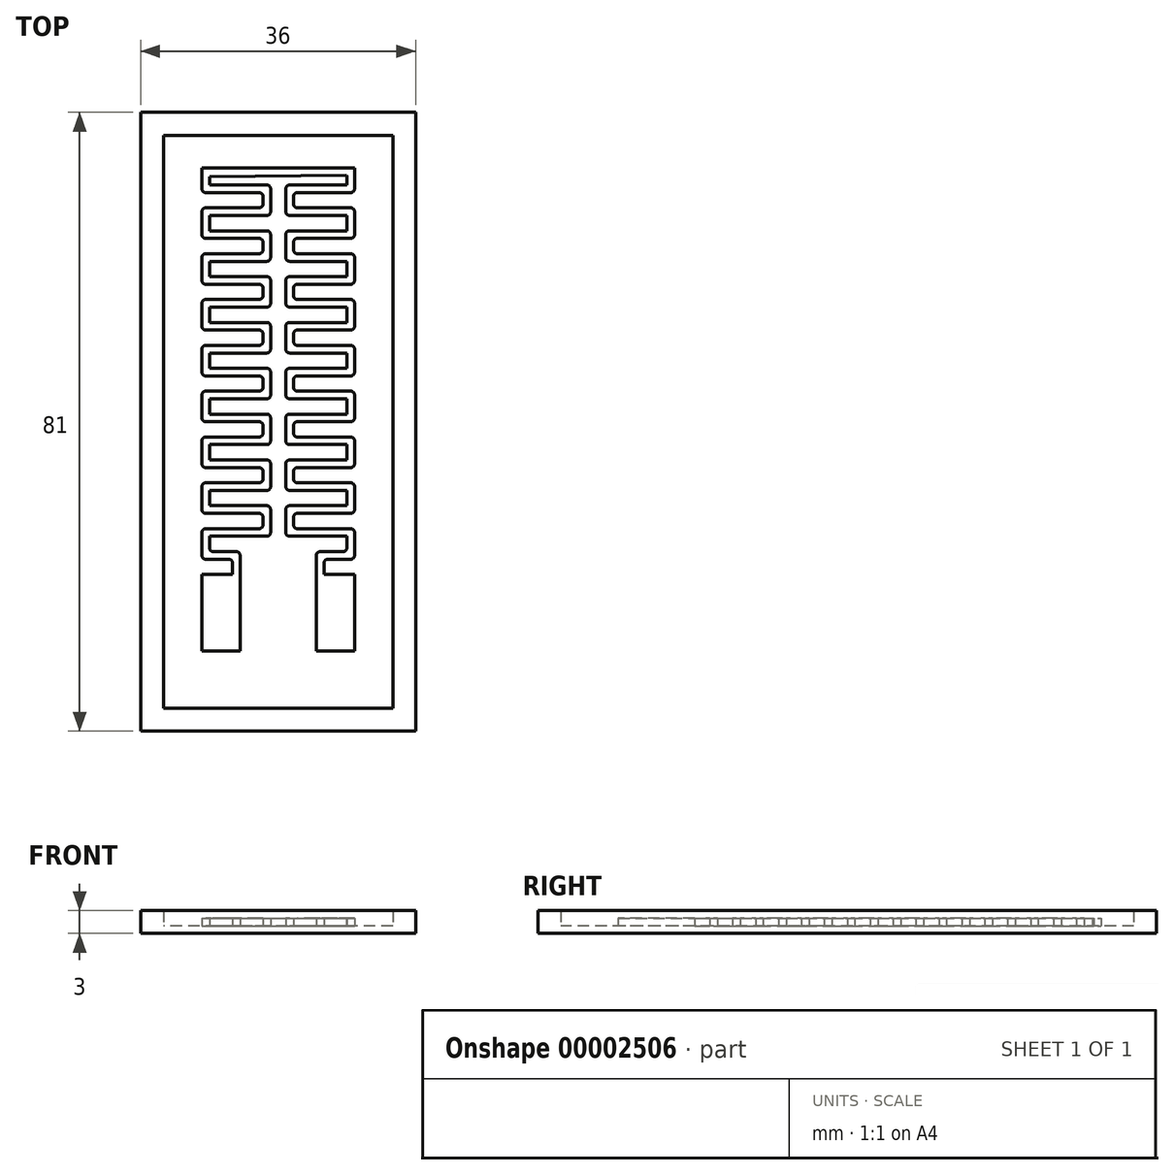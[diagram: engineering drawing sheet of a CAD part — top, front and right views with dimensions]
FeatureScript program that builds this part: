
annotation { "Feature Type Name" : "Feature", "Feature Type Description" : "" }
export const myFeature = defineFeature(function(context is Context, id is Id, definition is map)
    precondition{}
    {
        {
            var Q0;
            Q0=qCreatedBy(makeId("Top.planeOp"),FACE);
            var sketch = newSketch(context, id + "F0", { "sketchPlane" : qUnion([Q0])});
            skLineSegment(sketch, "E0.rect.bottom", {"start": v(15, 37.5) * mm, "end": v(-15, 37.5) * mm});
            skLineSegment(sketch, "E0.rect.top", {"start": v(15, -37.5) * mm, "end": v(-15, -37.5) * mm});
            skLineSegment(sketch, "E0.rect.left", {"start": v(15, 37.5) * mm, "end": v(15, -37.5) * mm});
            skLineSegment(sketch, "E0.rect.right", {"start": v(-15, 37.5) * mm, "end": v(-15, -37.5) * mm});
            skPoint(sketch, "E0.rect.middle", {"position": v(0, 0) * mm});
            skLineSegment(sketch, "E1", {"start": v(0, 0) * mm, "end": v(0, 17.9) * mm, "construction": true});
            skLineSegment(sketch, "E2.bottom", {"start": v(-10, -20) * mm, "end": v(-6, -20) * mm});
            skLineSegment(sketch, "E2.top", {"start": v(-10, -30) * mm, "end": v(-5, -30) * mm});
            skLineSegment(sketch, "E2.left", {"start": v(-10, -20) * mm, "end": v(-10, -30) * mm});
            skLineSegment(sketch, "E2.right", {"start": v(-5, -20) * mm, "end": v(-5, -30) * mm});
            skLineSegment(sketch, "E3", {"start": v(-5, -20) * mm, "end": v(-5, 28) * mm, "construction": true});
            skLineSegment(sketch, "E4", {"start": v(-4, 29) * mm, "end": v(0, 29) * mm, "construction": true});
            skLineSegment(sketch, "E5", {"start": v(-6, -20) * mm, "end": v(-6, 29) * mm, "construction": true});
            skLineSegment(sketch, "E6", {"start": v(-5, 30) * mm, "end": v(0, 30) * mm, "construction": true});
            skPoint(sketch, "E7.visualSharp", {"position": v(-6, 30) * mm});
            skArc(sketch, "E7.filletArc", {"start": v(-5, 30) * mm, "mid": v(-5.7, 29.7) * mm, "end": v(-6, 29) * mm, "construction": true});
            skArc(sketch, "E8.filletArc", {"start": v(-4, 29) * mm, "mid": v(-4.7, 28.7) * mm, "end": v(-5, 28) * mm, "construction": true});
            skLineSegment(sketch, "E9.0.MirrorCS", {"start": v(10, -30) * mm, "end": v(5, -30) * mm});
            skArc(sketch, "E9.1.MirrorCS", {"start": v(4, 29) * mm, "mid": v(4.7, 28.7) * mm, "end": v(5, 28) * mm, "construction": true});
            skArc(sketch, "E9.2.MirrorCS", {"start": v(5, 30) * mm, "mid": v(5.7, 29.7) * mm, "end": v(6, 29) * mm, "construction": true});
            skLineSegment(sketch, "E9.3.MirrorCS", {"start": v(10, -20) * mm, "end": v(6, -20) * mm});
            skLineSegment(sketch, "E9.4.MirrorCS", {"start": v(4, 29) * mm, "end": v(0, 29) * mm, "construction": true});
            skLineSegment(sketch, "E9.5.MirrorCS", {"start": v(5, 30) * mm, "end": v(0, 30) * mm, "construction": true});
            skPoint(sketch, "E9.6.MirrorP", {"position": v(6, 30) * mm});
            skLineSegment(sketch, "E9.8.MirrorCS", {"start": v(5, -20) * mm, "end": v(5, -30) * mm});
            skPoint(sketch, "E9.9.MirrorP", {"position": v(5, 29) * mm});
            skLineSegment(sketch, "E9.10.MirrorCS", {"start": v(6, -20) * mm, "end": v(6, 29) * mm, "construction": true});
            skLineSegment(sketch, "E9.11.MirrorCS", {"start": v(10, -20) * mm, "end": v(10, -30) * mm});
            skLineSegment(sketch, "E9.12.MirrorCS", {"start": v(5, -20) * mm, "end": v(5, 28) * mm, "construction": true});
            skLineSegment(sketch, "E10.0", {"start": v(18, 40.5) * mm, "end": v(-18, 40.5) * mm});
            skLineSegment(sketch, "E10.1", {"start": v(18, 40.5) * mm, "end": v(18, -40.5) * mm});
            skLineSegment(sketch, "E10.2", {"start": v(18, -40.5) * mm, "end": v(-18, -40.5) * mm});
            skLineSegment(sketch, "E10.3", {"start": v(-18, 40.5) * mm, "end": v(-18, -40.5) * mm});
            skLineSegment(sketch, "E11", {"start": v(-5, -20) * mm, "end": v(-5, -17.5) * mm});
            skLineSegment(sketch, "E12", {"start": v(-5.5, -17) * mm, "end": v(-8.5, -17) * mm});
            skLineSegment(sketch, "E13", {"start": v(-6, -20) * mm, "end": v(-6, -18.5) * mm});
            skLineSegment(sketch, "E14", {"start": v(-6.5, -18) * mm, "end": v(-9.5, -18) * mm});
            skLineSegment(sketch, "E15", {"start": v(-9, -16.5) * mm, "end": v(-9, -15) * mm});
            skLineSegment(sketch, "E16", {"start": v(-10, -17.5) * mm, "end": v(-10, -14.5) * mm});
            skLineSegment(sketch, "E17", {"start": v(0, 0) * mm, "end": v(0, -26.26) * mm, "construction": true});
            skLineSegment(sketch, "E18", {"start": v(-1, -22.87) * mm, "end": v(-1, 3.47) * mm, "construction": true});
            skLineSegment(sketch, "E19", {"start": v(-9, -15) * mm, "end": v(-1.5, -15) * mm});
            skLineSegment(sketch, "E20", {"start": v(-9.5, -14) * mm, "end": v(-2.5, -14) * mm});
            skLineSegment(sketch, "E21", {"start": v(-1, -14.5) * mm, "end": v(-1, -11.5) * mm});
            skLineSegment(sketch, "E22", {"start": v(-1.5, -11) * mm, "end": v(-9, -11) * mm});
            skLineSegment(sketch, "E23", {"start": v(-2, -13.5) * mm, "end": v(-2, -12.5) * mm});
            skLineSegment(sketch, "E24", {"start": v(-2.5, -12) * mm, "end": v(-9.5, -12) * mm});
            skLineSegment(sketch, "E25", {"start": v(-10, -11.5) * mm, "end": v(-10, -11) * mm});
            skPoint(sketch, "E26.visualSharp", {"position": v(-5, -17) * mm});
            skArc(sketch, "E26.filletArc", {"start": v(-5, -17.5) * mm, "mid": v(-5.15, -17.15) * mm, "end": v(-5.5, -17) * mm});
            skPoint(sketch, "E27.visualSharp", {"position": v(-6, -18) * mm});
            skArc(sketch, "E27.filletArc", {"start": v(-6, -18.5) * mm, "mid": v(-6.15, -18.15) * mm, "end": v(-6.5, -18) * mm});
            skPoint(sketch, "E28.visualSharp", {"position": v(-10, -18) * mm});
            skArc(sketch, "E28.filletArc", {"start": v(-10, -17.5) * mm, "mid": v(-9.85, -17.85) * mm, "end": v(-9.5, -18) * mm});
            skPoint(sketch, "E29.visualSharp", {"position": v(-10, -14) * mm});
            skArc(sketch, "E29.filletArc", {"start": v(-9.5, -14) * mm, "mid": v(-9.85, -14.15) * mm, "end": v(-10, -14.5) * mm});
            skPoint(sketch, "E30.visualSharp", {"position": v(-1, -15) * mm});
            skArc(sketch, "E30.filletArc", {"start": v(-1.5, -15) * mm, "mid": v(-1.15, -14.85) * mm, "end": v(-1, -14.5) * mm});
            skPoint(sketch, "E31.visualSharp", {"position": v(-2, -14) * mm});
            skArc(sketch, "E31.filletArc", {"start": v(-2.5, -14) * mm, "mid": v(-2.15, -13.85) * mm, "end": v(-2, -13.5) * mm});
            skPoint(sketch, "E32.visualSharp", {"position": v(-2, -12) * mm});
            skArc(sketch, "E32.filletArc", {"start": v(-2, -12.5) * mm, "mid": v(-2.15, -12.15) * mm, "end": v(-2.5, -12) * mm});
            skPoint(sketch, "E33.visualSharp", {"position": v(-1, -11) * mm});
            skArc(sketch, "E33.filletArc", {"start": v(-1, -11.5) * mm, "mid": v(-1.15, -11.15) * mm, "end": v(-1.5, -11) * mm});
            skPoint(sketch, "E34.visualSharp", {"position": v(-10, -12) * mm});
            skArc(sketch, "E34.filletArc", {"start": v(-10, -11.5) * mm, "mid": v(-9.85, -11.85) * mm, "end": v(-9.5, -12) * mm});
            skPoint(sketch, "E35.visualSharp", {"position": v(-9, -17) * mm});
            skArc(sketch, "E35.filletArc", {"start": v(-9, -16.5) * mm, "mid": v(-8.85, -16.85) * mm, "end": v(-8.5, -17) * mm});
            skLineSegment(sketch, "E36.0.1.0", {"start": v(-10, -11.5) * mm, "end": v(-10, -8.5) * mm});
            skPoint(sketch, "E36.0.1.1", {"position": v(-10, -8) * mm});
            skArc(sketch, "E36.0.1.2", {"start": v(-9.5, -8) * mm, "mid": v(-9.85, -8.15) * mm, "end": v(-10, -8.5) * mm});
            skLineSegment(sketch, "E36.0.1.3", {"start": v(-9, -9) * mm, "end": v(-1.5, -9) * mm});
            skLineSegment(sketch, "E36.0.1.4", {"start": v(-9.5, -8) * mm, "end": v(-2.5, -8) * mm});
            skArc(sketch, "E36.0.1.5", {"start": v(-1.5, -9) * mm, "mid": v(-1.15, -8.85) * mm, "end": v(-1, -8.5) * mm});
            skArc(sketch, "E36.0.1.6", {"start": v(-2.5, -8) * mm, "mid": v(-2.15, -7.85) * mm, "end": v(-2, -7.5) * mm});
            skLineSegment(sketch, "E36.0.1.7", {"start": v(-2, -7.5) * mm, "end": v(-2, -6.5) * mm});
            skLineSegment(sketch, "E36.0.1.8", {"start": v(-1, -8.5) * mm, "end": v(-1, -5.5) * mm});
            skArc(sketch, "E36.0.1.9", {"start": v(-1, -5.5) * mm, "mid": v(-1.15, -5.15) * mm, "end": v(-1.5, -5) * mm});
            skArc(sketch, "E36.0.1.10", {"start": v(-2, -6.5) * mm, "mid": v(-2.15, -6.15) * mm, "end": v(-2.5, -6) * mm});
            skLineSegment(sketch, "E36.0.1.11", {"start": v(-2.5, -6) * mm, "end": v(-9.5, -6) * mm});
            skLineSegment(sketch, "E36.0.1.12", {"start": v(-1.5, -5) * mm, "end": v(-9, -5) * mm});
            skArc(sketch, "E36.0.1.13", {"start": v(-10, -5.5) * mm, "mid": v(-9.85, -5.85) * mm, "end": v(-9.5, -6) * mm});
            skLineSegment(sketch, "E36.0.1.14", {"start": v(-10, -5.5) * mm, "end": v(-10, -5) * mm});
            skLineSegment(sketch, "E36.0.2.0", {"start": v(-10, -5.5) * mm, "end": v(-10, -2.5) * mm});
            skPoint(sketch, "E36.0.2.1", {"position": v(-10, -2) * mm});
            skArc(sketch, "E36.0.2.2", {"start": v(-9.5, -2) * mm, "mid": v(-9.85, -2.15) * mm, "end": v(-10, -2.5) * mm});
            skLineSegment(sketch, "E36.0.2.3", {"start": v(-9, -3) * mm, "end": v(-1.5, -3) * mm});
            skLineSegment(sketch, "E36.0.2.4", {"start": v(-9.5, -2) * mm, "end": v(-2.5, -2) * mm});
            skArc(sketch, "E36.0.2.5", {"start": v(-1.5, -3) * mm, "mid": v(-1.15, -2.85) * mm, "end": v(-1, -2.5) * mm});
            skArc(sketch, "E36.0.2.6", {"start": v(-2.5, -2) * mm, "mid": v(-2.15, -1.85) * mm, "end": v(-2, -1.5) * mm});
            skLineSegment(sketch, "E36.0.2.7", {"start": v(-2, -1.5) * mm, "end": v(-2, -0.5) * mm});
            skLineSegment(sketch, "E36.0.2.8", {"start": v(-1, -2.5) * mm, "end": v(-1, 0.5) * mm});
            skArc(sketch, "E36.0.2.9", {"start": v(-1, 0.5) * mm, "mid": v(-1.15, 0.85) * mm, "end": v(-1.5, 1) * mm});
            skArc(sketch, "E36.0.2.10", {"start": v(-2, -0.5) * mm, "mid": v(-2.15, -0.15) * mm, "end": v(-2.5, 0) * mm});
            skLineSegment(sketch, "E36.0.2.11", {"start": v(-2.5, 0) * mm, "end": v(-9.5, 0) * mm});
            skLineSegment(sketch, "E36.0.2.12", {"start": v(-1.5, 1) * mm, "end": v(-9, 1) * mm});
            skArc(sketch, "E36.0.2.13", {"start": v(-10, 0.5) * mm, "mid": v(-9.85, 0.15) * mm, "end": v(-9.5, 0) * mm});
            skLineSegment(sketch, "E36.0.2.14", {"start": v(-10, 0.5) * mm, "end": v(-10, 1) * mm});
            skLineSegment(sketch, "E36.0.3.0", {"start": v(-10, 0.5) * mm, "end": v(-10, 3.5) * mm});
            skPoint(sketch, "E36.0.3.1", {"position": v(-10, 4) * mm});
            skArc(sketch, "E36.0.3.2", {"start": v(-9.5, 4) * mm, "mid": v(-9.85, 3.85) * mm, "end": v(-10, 3.5) * mm});
            skLineSegment(sketch, "E36.0.3.3", {"start": v(-9, 3) * mm, "end": v(-1.5, 3) * mm});
            skLineSegment(sketch, "E36.0.3.4", {"start": v(-9.5, 4) * mm, "end": v(-2.5, 4) * mm});
            skArc(sketch, "E36.0.3.5", {"start": v(-1.5, 3) * mm, "mid": v(-1.15, 3.15) * mm, "end": v(-1, 3.5) * mm});
            skArc(sketch, "E36.0.3.6", {"start": v(-2.5, 4) * mm, "mid": v(-2.15, 4.15) * mm, "end": v(-2, 4.5) * mm});
            skLineSegment(sketch, "E36.0.3.7", {"start": v(-2, 4.5) * mm, "end": v(-2, 5.5) * mm});
            skLineSegment(sketch, "E36.0.3.8", {"start": v(-1, 3.5) * mm, "end": v(-1, 6.5) * mm});
            skArc(sketch, "E36.0.3.9", {"start": v(-1, 6.5) * mm, "mid": v(-1.15, 6.85) * mm, "end": v(-1.5, 7) * mm});
            skArc(sketch, "E36.0.3.10", {"start": v(-2, 5.5) * mm, "mid": v(-2.15, 5.85) * mm, "end": v(-2.5, 6) * mm});
            skLineSegment(sketch, "E36.0.3.11", {"start": v(-2.5, 6) * mm, "end": v(-9.5, 6) * mm});
            skLineSegment(sketch, "E36.0.3.12", {"start": v(-1.5, 7) * mm, "end": v(-9, 7) * mm});
            skArc(sketch, "E36.0.3.13", {"start": v(-10, 6.5) * mm, "mid": v(-9.85, 6.15) * mm, "end": v(-9.5, 6) * mm});
            skLineSegment(sketch, "E36.0.3.14", {"start": v(-10, 6.5) * mm, "end": v(-10, 7) * mm});
            skLineSegment(sketch, "E36.0.4.0", {"start": v(-10, 6.5) * mm, "end": v(-10, 9.5) * mm});
            skPoint(sketch, "E36.0.4.1", {"position": v(-10, 10) * mm});
            skArc(sketch, "E36.0.4.2", {"start": v(-9.5, 10) * mm, "mid": v(-9.85, 9.85) * mm, "end": v(-10, 9.5) * mm});
            skLineSegment(sketch, "E36.0.4.3", {"start": v(-9, 9) * mm, "end": v(-1.5, 9) * mm});
            skLineSegment(sketch, "E36.0.4.4", {"start": v(-9.5, 10) * mm, "end": v(-2.5, 10) * mm});
            skArc(sketch, "E36.0.4.5", {"start": v(-1.5, 9) * mm, "mid": v(-1.15, 9.15) * mm, "end": v(-1, 9.5) * mm});
            skArc(sketch, "E36.0.4.6", {"start": v(-2.5, 10) * mm, "mid": v(-2.15, 10.15) * mm, "end": v(-2, 10.5) * mm});
            skLineSegment(sketch, "E36.0.4.7", {"start": v(-2, 10.5) * mm, "end": v(-2, 11.5) * mm});
            skLineSegment(sketch, "E36.0.4.8", {"start": v(-1, 9.5) * mm, "end": v(-1, 12.5) * mm});
            skArc(sketch, "E36.0.4.9", {"start": v(-1, 12.5) * mm, "mid": v(-1.15, 12.85) * mm, "end": v(-1.5, 13) * mm});
            skArc(sketch, "E36.0.4.10", {"start": v(-2, 11.5) * mm, "mid": v(-2.15, 11.85) * mm, "end": v(-2.5, 12) * mm});
            skLineSegment(sketch, "E36.0.4.11", {"start": v(-2.5, 12) * mm, "end": v(-9.5, 12) * mm});
            skLineSegment(sketch, "E36.0.4.12", {"start": v(-1.5, 13) * mm, "end": v(-9, 13) * mm});
            skArc(sketch, "E36.0.4.13", {"start": v(-10, 12.5) * mm, "mid": v(-9.85, 12.15) * mm, "end": v(-9.5, 12) * mm});
            skLineSegment(sketch, "E36.0.4.14", {"start": v(-10, 12.5) * mm, "end": v(-10, 13) * mm});
            skLineSegment(sketch, "E36.direction1", {"start": v(-10, -17.5) * mm, "end": v(15, -17.5) * mm, "construction": true});
            skLineSegment(sketch, "E36.direction2", {"start": v(-10, -17.5) * mm, "end": v(-10, -11.5) * mm, "construction": true});
            skArc(sketch, "E37.0.MirrorCS", {"start": v(10, -11.5) * mm, "mid": v(9.85, -11.85) * mm, "end": v(9.5, -12) * mm});
            skLineSegment(sketch, "E37.1.MirrorCS", {"start": v(10, -11.5) * mm, "end": v(10, -11) * mm});
            skArc(sketch, "E37.2.MirrorCS", {"start": v(10, -17.5) * mm, "mid": v(9.85, -17.85) * mm, "end": v(9.5, -18) * mm});
            skArc(sketch, "E37.3.MirrorCS", {"start": v(9, -16.5) * mm, "mid": v(8.85, -16.85) * mm, "end": v(8.5, -17) * mm});
            skArc(sketch, "E37.4.MirrorCS", {"start": v(1.5, 3) * mm, "mid": v(1.15, 3.15) * mm, "end": v(1, 3.5) * mm});
            skArc(sketch, "E37.5.MirrorCS", {"start": v(2.5, 16) * mm, "mid": v(2.15, 16.15) * mm, "end": v(2, 16.5) * mm});
            skLineSegment(sketch, "E37.6.MirrorCS", {"start": v(10, -5.5) * mm, "end": v(10, -5) * mm});
            skLineSegment(sketch, "E37.7.MirrorCS", {"start": v(2, 16.5) * mm, "end": v(2, 17.5) * mm});
            skLineSegment(sketch, "E37.8.MirrorCS", {"start": v(2, 4.5) * mm, "end": v(2, 5.5) * mm});
            skArc(sketch, "E37.9.MirrorCS", {"start": v(10, 24.5) * mm, "mid": v(9.85, 24.15) * mm, "end": v(9.5, 24) * mm});
            skLineSegment(sketch, "E37.10.MirrorCS", {"start": v(10, 24.5) * mm, "end": v(10, 25) * mm});
            skArc(sketch, "E37.11.MirrorCS", {"start": v(2.5, -14) * mm, "mid": v(2.15, -13.85) * mm, "end": v(2, -13.5) * mm});
            skArc(sketch, "E37.12.MirrorCS", {"start": v(1.5, -15) * mm, "mid": v(1.15, -14.85) * mm, "end": v(1, -14.5) * mm});
            skArc(sketch, "E37.13.MirrorCS", {"start": v(10, 0.5) * mm, "mid": v(9.85, 0.15) * mm, "end": v(9.5, 0) * mm});
            skLineSegment(sketch, "E37.14.MirrorCS", {"start": v(10, 0.5) * mm, "end": v(10, 1) * mm});
            skArc(sketch, "E37.15.MirrorCS", {"start": v(10, -5.5) * mm, "mid": v(9.85, -5.85) * mm, "end": v(9.5, -6) * mm});
            skArc(sketch, "E37.16.MirrorCS", {"start": v(10, 18.5) * mm, "mid": v(9.85, 18.15) * mm, "end": v(9.5, 18) * mm});
            skLineSegment(sketch, "E37.17.MirrorCS", {"start": v(10, 18.5) * mm, "end": v(10, 19) * mm});
            skArc(sketch, "E37.18.MirrorCS", {"start": v(2, 5.5) * mm, "mid": v(2.15, 5.85) * mm, "end": v(2.5, 6) * mm});
            skLineSegment(sketch, "E37.19.MirrorCS", {"start": v(10, 12.5) * mm, "end": v(10, 13) * mm});
            skArc(sketch, "E37.20.MirrorCS", {"start": v(1, -5.5) * mm, "mid": v(1.15, -5.15) * mm, "end": v(1.5, -5) * mm});
            skArc(sketch, "E37.21.MirrorCS", {"start": v(10, 6.5) * mm, "mid": v(9.85, 6.15) * mm, "end": v(9.5, 6) * mm});
            skArc(sketch, "E37.22.MirrorCS", {"start": v(2.5, 4) * mm, "mid": v(2.15, 4.15) * mm, "end": v(2, 4.5) * mm});
            skArc(sketch, "E37.23.MirrorCS", {"start": v(10, 12.5) * mm, "mid": v(9.85, 12.15) * mm, "end": v(9.5, 12) * mm});
            skLineSegment(sketch, "E37.24.MirrorCS", {"start": v(10, 6.5) * mm, "end": v(10, 7) * mm});
            skArc(sketch, "E37.25.MirrorCS", {"start": v(2, -6.5) * mm, "mid": v(2.15, -6.15) * mm, "end": v(2.5, -6) * mm});
            skArc(sketch, "E37.26.MirrorCS", {"start": v(2, 23.5) * mm, "mid": v(2.15, 23.85) * mm, "end": v(2.5, 24) * mm});
            skArc(sketch, "E37.27.MirrorCS", {"start": v(2.5, 10) * mm, "mid": v(2.15, 10.15) * mm, "end": v(2, 10.5) * mm});
            skArc(sketch, "E37.28.MirrorCS", {"start": v(9.5, -2) * mm, "mid": v(9.85, -2.15) * mm, "end": v(10, -2.5) * mm});
            skArc(sketch, "E37.29.MirrorCS", {"start": v(10, 30.5) * mm, "mid": v(9.85, 30.15) * mm, "end": v(9.5, 30) * mm});
            skArc(sketch, "E37.30.MirrorCS", {"start": v(1, 18.5) * mm, "mid": v(1.15, 18.85) * mm, "end": v(1.5, 19) * mm});
            skLineSegment(sketch, "E37.31.MirrorCS", {"start": v(2, 10.5) * mm, "end": v(2, 11.5) * mm});
            skArc(sketch, "E37.32.MirrorCS", {"start": v(2, 29.5) * mm, "mid": v(2.15, 29.85) * mm, "end": v(2.5, 30) * mm});
            skArc(sketch, "E37.33.MirrorCS", {"start": v(1, -11.5) * mm, "mid": v(1.15, -11.15) * mm, "end": v(1.5, -11) * mm});
            skArc(sketch, "E37.34.MirrorCS", {"start": v(9.5, 4) * mm, "mid": v(9.85, 3.85) * mm, "end": v(10, 3.5) * mm});
            skArc(sketch, "E37.35.MirrorCS", {"start": v(1.5, 9) * mm, "mid": v(1.15, 9.15) * mm, "end": v(1, 9.5) * mm});
            skArc(sketch, "E37.36.MirrorCS", {"start": v(1, 24.5) * mm, "mid": v(1.15, 24.85) * mm, "end": v(1.5, 25) * mm});
            skLineSegment(sketch, "E37.37.MirrorCS", {"start": v(10, 30.5) * mm, "end": v(10, 31) * mm});
            skArc(sketch, "E37.40.MirrorCS", {"start": v(1.5, -3) * mm, "mid": v(1.15, -2.85) * mm, "end": v(1, -2.5) * mm});
            skArc(sketch, "E37.41.MirrorCS", {"start": v(1, 12.5) * mm, "mid": v(1.15, 12.85) * mm, "end": v(1.5, 13) * mm});
            skLineSegment(sketch, "E37.42.MirrorCS", {"start": v(2, -13.5) * mm, "end": v(2, -12.5) * mm});
            skArc(sketch, "E37.43.MirrorCS", {"start": v(2.5, -2) * mm, "mid": v(2.15, -1.85) * mm, "end": v(2, -1.5) * mm});
            skArc(sketch, "E37.44.MirrorCS", {"start": v(2, 11.5) * mm, "mid": v(2.15, 11.85) * mm, "end": v(2.5, 12) * mm});
            skLineSegment(sketch, "E37.45.MirrorCS", {"start": v(9, -16.5) * mm, "end": v(9, -15) * mm});
            skArc(sketch, "E37.46.MirrorCS", {"start": v(9.5, 22) * mm, "mid": v(9.85, 21.85) * mm, "end": v(10, 21.5) * mm});
            skArc(sketch, "E37.47.MirrorCS", {"start": v(9.5, 28) * mm, "mid": v(9.85, 27.85) * mm, "end": v(10, 27.5) * mm});
            skArc(sketch, "E37.48.MirrorCS", {"start": v(1, 6.5) * mm, "mid": v(1.15, 6.85) * mm, "end": v(1.5, 7) * mm});
            skArc(sketch, "E37.49.MirrorCS", {"start": v(6, -18.5) * mm, "mid": v(6.15, -18.15) * mm, "end": v(6.5, -18) * mm});
            skArc(sketch, "E37.50.MirrorCS", {"start": v(9.5, 10) * mm, "mid": v(9.85, 9.85) * mm, "end": v(10, 9.5) * mm});
            skArc(sketch, "E37.51.MirrorCS", {"start": v(2.5, 22) * mm, "mid": v(2.15, 22.15) * mm, "end": v(2, 22.5) * mm});
            skLineSegment(sketch, "E37.52.MirrorCS", {"start": v(2, -1.5) * mm, "end": v(2, -0.5) * mm});
            skArc(sketch, "E37.53.MirrorCS", {"start": v(2, -0.5) * mm, "mid": v(2.15, -0.15) * mm, "end": v(2.5, 0) * mm});
            skArc(sketch, "E37.54.MirrorCS", {"start": v(2, -12.5) * mm, "mid": v(2.15, -12.15) * mm, "end": v(2.5, -12) * mm});
            skArc(sketch, "E37.55.MirrorCS", {"start": v(2.5, -8) * mm, "mid": v(2.15, -7.85) * mm, "end": v(2, -7.5) * mm});
            skArc(sketch, "E37.56.MirrorCS", {"start": v(1.5, -9) * mm, "mid": v(1.15, -8.85) * mm, "end": v(1, -8.5) * mm});
            skArc(sketch, "E37.57.MirrorCS", {"start": v(5, -17.5) * mm, "mid": v(5.15, -17.15) * mm, "end": v(5.5, -17) * mm});
            skLineSegment(sketch, "E37.58.MirrorCS", {"start": v(2, 22.5) * mm, "end": v(2, 23.5) * mm});
            skArc(sketch, "E37.59.MirrorCS", {"start": v(1.5, 27) * mm, "mid": v(1.15, 27.15) * mm, "end": v(1, 27.5) * mm});
            skArc(sketch, "E37.60.MirrorCS", {"start": v(9.5, -8) * mm, "mid": v(9.85, -8.15) * mm, "end": v(10, -8.5) * mm});
            skArc(sketch, "E37.61.MirrorCS", {"start": v(2, 17.5) * mm, "mid": v(2.15, 17.85) * mm, "end": v(2.5, 18) * mm});
            skLineSegment(sketch, "E37.62.MirrorCS", {"start": v(2, -7.5) * mm, "end": v(2, -6.5) * mm});
            skArc(sketch, "E37.63.MirrorCS", {"start": v(1, 0.5) * mm, "mid": v(1.15, 0.85) * mm, "end": v(1.5, 1) * mm});
            skArc(sketch, "E37.64.MirrorCS", {"start": v(2.5, 28) * mm, "mid": v(2.15, 28.15) * mm, "end": v(2, 28.5) * mm});
            skArc(sketch, "E37.65.MirrorCS", {"start": v(9.5, 16) * mm, "mid": v(9.85, 15.85) * mm, "end": v(10, 15.5) * mm});
            skArc(sketch, "E37.66.MirrorCS", {"start": v(9.5, -14) * mm, "mid": v(9.85, -14.15) * mm, "end": v(10, -14.5) * mm});
            skLineSegment(sketch, "E37.67.MirrorCS", {"start": v(2, 28.5) * mm, "end": v(2, 29.5) * mm});
            skArc(sketch, "E37.68.MirrorCS", {"start": v(1.5, 21) * mm, "mid": v(1.15, 21.15) * mm, "end": v(1, 21.5) * mm});
            skArc(sketch, "E37.69.MirrorCS", {"start": v(1, 30.5) * mm, "mid": v(1.15, 30.85) * mm, "end": v(1.5, 31) * mm});
            skArc(sketch, "E37.70.MirrorCS", {"start": v(1.5, 15) * mm, "mid": v(1.15, 15.15) * mm, "end": v(1, 15.5) * mm});
            skLineSegment(sketch, "E37.74.MirrorCS", {"start": v(10, -17.5) * mm, "end": v(10, -11.5) * mm, "construction": true});
            skLineSegment(sketch, "E37.75.MirrorCS", {"start": v(1, -14.5) * mm, "end": v(1, -11.5) * mm});
            skPoint(sketch, "E37.77.MirrorP", {"position": v(10, 22) * mm});
            skLineSegment(sketch, "E37.78.MirrorCS", {"start": v(1.5, 31) * mm, "end": v(9, 31) * mm});
            skLineSegment(sketch, "E37.79.MirrorCS", {"start": v(1, 15.5) * mm, "end": v(1, 18.5) * mm});
            skLineSegment(sketch, "E37.80.MirrorCS", {"start": v(9.5, 4) * mm, "end": v(2.5, 4) * mm});
            skLineSegment(sketch, "E37.81.MirrorCS", {"start": v(9, -15) * mm, "end": v(1.5, -15) * mm});
            skPoint(sketch, "E37.82.MirrorP", {"position": v(1, -15) * mm});
            skLineSegment(sketch, "E37.83.MirrorCS", {"start": v(9, -3) * mm, "end": v(1.5, -3) * mm});
            skLineSegment(sketch, "E37.84.MirrorCS", {"start": v(10, -11.5) * mm, "end": v(10, -8.5) * mm});
            skLineSegment(sketch, "E37.85.MirrorCS", {"start": v(9.5, -14) * mm, "end": v(2.5, -14) * mm});
            skLineSegment(sketch, "E37.86.MirrorCS", {"start": v(2.5, 24) * mm, "end": v(9.5, 24) * mm});
            skLineSegment(sketch, "E37.87.MirrorCS", {"start": v(9.5, 10) * mm, "end": v(2.5, 10) * mm});
            skLineSegment(sketch, "E37.88.MirrorCS", {"start": v(1, 21.5) * mm, "end": v(1, 24.5) * mm});
            skPoint(sketch, "E37.90.MirrorP", {"position": v(10, -14) * mm});
            skLineSegment(sketch, "E37.91.MirrorCS", {"start": v(2.5, 30) * mm, "end": v(9.5, 30) * mm});
            skLineSegment(sketch, "E37.92.MirrorCS", {"start": v(9, 3) * mm, "end": v(1.5, 3) * mm});
            skLineSegment(sketch, "E37.93.MirrorCS", {"start": v(10, -5.5) * mm, "end": v(10, -2.5) * mm});
            skLineSegment(sketch, "E37.94.MirrorCS", {"start": v(1.5, 25) * mm, "end": v(9, 25) * mm});
            skPoint(sketch, "E37.95.MirrorP", {"position": v(2, -14) * mm});
            skLineSegment(sketch, "E37.96.MirrorCS", {"start": v(2.5, 18) * mm, "end": v(9.5, 18) * mm});
            skLineSegment(sketch, "E37.97.MirrorCS", {"start": v(9, -9) * mm, "end": v(1.5, -9) * mm});
            skLineSegment(sketch, "E37.98.MirrorCS", {"start": v(1.5, -11) * mm, "end": v(9, -11) * mm});
            skPoint(sketch, "E37.99.MirrorP", {"position": v(10, -2) * mm});
            skLineSegment(sketch, "E37.100.MirrorCS", {"start": v(9.5, -8) * mm, "end": v(2.5, -8) * mm});
            skLineSegment(sketch, "E37.101.MirrorCS", {"start": v(1, 3.5) * mm, "end": v(1, 6.5) * mm});
            skLineSegment(sketch, "E37.102.MirrorCS", {"start": v(1.5, 19) * mm, "end": v(9, 19) * mm});
            skLineSegment(sketch, "E37.103.MirrorCS", {"start": v(1.5, -5) * mm, "end": v(9, -5) * mm});
            skLineSegment(sketch, "E37.104.MirrorCS", {"start": v(2.5, 12) * mm, "end": v(9.5, 12) * mm});
            skLineSegment(sketch, "E37.105.MirrorCS", {"start": v(1.5, 13) * mm, "end": v(9, 13) * mm});
            skLineSegment(sketch, "E37.106.MirrorCS", {"start": v(10, 0.5) * mm, "end": v(10, 3.5) * mm});
            skLineSegment(sketch, "E37.107.MirrorCS", {"start": v(10, -17.5) * mm, "end": v(10, -14.5) * mm});
            skLineSegment(sketch, "E37.108.MirrorCS", {"start": v(10, 24.5) * mm, "end": v(10, 27.5) * mm});
            skPoint(sketch, "E37.109.MirrorP", {"position": v(2, -12) * mm});
            skLineSegment(sketch, "E37.110.MirrorCS", {"start": v(9.5, 28) * mm, "end": v(2.5, 28) * mm});
            skLineSegment(sketch, "E37.111.MirrorCS", {"start": v(1, -8.5) * mm, "end": v(1, -5.5) * mm});
            skLineSegment(sketch, "E37.112.MirrorCS", {"start": v(6.5, -18) * mm, "end": v(9.5, -18) * mm});
            skLineSegment(sketch, "E37.113.MirrorCS", {"start": v(2.5, -6) * mm, "end": v(9.5, -6) * mm});
            skPoint(sketch, "E37.114.MirrorP", {"position": v(9, -17) * mm});
            skLineSegment(sketch, "E37.115.MirrorCS", {"start": v(1, 27.5) * mm, "end": v(1, 30.5) * mm});
            skPoint(sketch, "E37.116.MirrorP", {"position": v(6, -18) * mm});
            skLineSegment(sketch, "E37.117.MirrorCS", {"start": v(9.5, 16) * mm, "end": v(2.5, 16) * mm});
            skPoint(sketch, "E37.118.MirrorP", {"position": v(10, 4) * mm});
            skLineSegment(sketch, "E37.119.MirrorCS", {"start": v(1, -2.5) * mm, "end": v(1, 0.5) * mm});
            skLineSegment(sketch, "E37.120.MirrorCS", {"start": v(1.5, 7) * mm, "end": v(9, 7) * mm});
            skPoint(sketch, "E37.121.MirrorP", {"position": v(10, -8) * mm});
            skPoint(sketch, "E37.122.MirrorP", {"position": v(10, -18) * mm});
            skLineSegment(sketch, "E37.123.MirrorCS", {"start": v(2.5, -12) * mm, "end": v(9.5, -12) * mm});
            skLineSegment(sketch, "E37.124.MirrorCS", {"start": v(10, 6.5) * mm, "end": v(10, 9.5) * mm});
            skLineSegment(sketch, "E37.125.MirrorCS", {"start": v(10, 18.5) * mm, "end": v(10, 21.5) * mm});
            skPoint(sketch, "E37.126.MirrorP", {"position": v(10, 16) * mm});
            skPoint(sketch, "E37.127.MirrorP", {"position": v(10, -12) * mm});
            skLineSegment(sketch, "E37.128.MirrorCS", {"start": v(9, 9) * mm, "end": v(1.5, 9) * mm});
            skPoint(sketch, "E37.129.MirrorP", {"position": v(5, -17) * mm});
            skLineSegment(sketch, "E37.130.MirrorCS", {"start": v(5.5, -17) * mm, "end": v(8.5, -17) * mm});
            skLineSegment(sketch, "E37.131.MirrorCS", {"start": v(2.5, 0) * mm, "end": v(9.5, 0) * mm});
            skLineSegment(sketch, "E37.132.MirrorCS", {"start": v(10, 12.5) * mm, "end": v(10, 15.5) * mm});
            skLineSegment(sketch, "E37.133.MirrorCS", {"start": v(9, 21) * mm, "end": v(1.5, 21) * mm});
            skLineSegment(sketch, "E37.134.MirrorCS", {"start": v(1, 9.5) * mm, "end": v(1, 12.5) * mm});
            skLineSegment(sketch, "E37.135.MirrorCS", {"start": v(9.5, -2) * mm, "end": v(2.5, -2) * mm});
            skPoint(sketch, "E37.136.MirrorP", {"position": v(10, 10) * mm});
            skLineSegment(sketch, "E37.138.MirrorCS", {"start": v(9, 27) * mm, "end": v(1.5, 27) * mm});
            skLineSegment(sketch, "E37.139.MirrorCS", {"start": v(2.5, 6) * mm, "end": v(9.5, 6) * mm});
            skLineSegment(sketch, "E37.140.MirrorCS", {"start": v(9.5, 22) * mm, "end": v(2.5, 22) * mm});
            skLineSegment(sketch, "E37.141.MirrorCS", {"start": v(9, 15) * mm, "end": v(1.5, 15) * mm});
            skLineSegment(sketch, "E37.142.MirrorCS", {"start": v(1.5, 1) * mm, "end": v(9, 1) * mm});
            skPoint(sketch, "E37.143.MirrorP", {"position": v(10, 28) * mm});
            skPoint(sketch, "E37.144.MirrorP", {"position": v(1, -11) * mm});
            skLineSegment(sketch, "E38", {"start": v(-10, 31) * mm, "end": v(-10, 33.22) * mm});
            skLineSegment(sketch, "E39", {"start": v(-10, 33.22) * mm, "end": v(7.5, 33.22) * mm});
            skLineSegment(sketch, "E40", {"start": v(-9, 31) * mm, "end": v(-9, 32.11) * mm});
            skLineSegment(sketch, "E41", {"start": v(-9, 32.11) * mm, "end": v(9.03, 32.26) * mm});
            skLineSegment(sketch, "E42", {"start": v(10, 31) * mm, "end": v(10, 33.22) * mm});
            skLineSegment(sketch, "E43", {"start": v(9, 31) * mm, "end": v(9.03, 32.26) * mm});
            skLineSegment(sketch, "E44", {"start": v(10, 33.22) * mm, "end": v(7.5, 33.22) * mm});
            skLineSegment(sketch, "E45", {"start": v(9, 27) * mm, "end": v(9, 25) * mm});
            skLineSegment(sketch, "E46", {"start": v(-9, 27) * mm, "end": v(-9, 25) * mm});
            skLineSegment(sketch, "E47", {"start": v(9, 21) * mm, "end": v(9, 19) * mm});
            skLineSegment(sketch, "E48", {"start": v(-9, 21) * mm, "end": v(-9, 19) * mm});
            skLineSegment(sketch, "E49", {"start": v(-9, 15) * mm, "end": v(-9, 13) * mm});
            skLineSegment(sketch, "E50", {"start": v(9, 15) * mm, "end": v(9, 13) * mm});
            skLineSegment(sketch, "E51", {"start": v(9, 9) * mm, "end": v(9, 7) * mm});
            skLineSegment(sketch, "E52", {"start": v(-9, 9) * mm, "end": v(-9, 7) * mm});
            skLineSegment(sketch, "E53", {"start": v(-9, 3) * mm, "end": v(-9, 1) * mm});
            skLineSegment(sketch, "E54", {"start": v(9, 3) * mm, "end": v(9, 1) * mm});
            skLineSegment(sketch, "E55", {"start": v(9, -3) * mm, "end": v(9, -5) * mm});
            skLineSegment(sketch, "E56", {"start": v(-9, -3) * mm, "end": v(-9, -5) * mm});
            skLineSegment(sketch, "E57", {"start": v(-9, -9) * mm, "end": v(-9, -11) * mm});
            skLineSegment(sketch, "E58", {"start": v(9, -9) * mm, "end": v(9, -11) * mm});
            skSolve(sketch);
        }
        {
            var Q0;
            Q0=makeQuery(id+"F0.imprint","IMPRINT",FACE,{"disambiguationData":[TD([[makeQuery(id+"F0.imprint","IMPRINT",EDGE,{"derivedFrom":sQuery(id+"F0.wireOp",EDGE,"E0.rect.bottom")}),-1.0]])]});
            extrude(context, id + "F1", {"entities" : qUnion([Q0]), "depth" : 2 * mm});
        }
        {
            var Q0;
            Q0=makeQuery(id+"F0.imprint","IMPRINT",FACE,{"disambiguationData":[TD([[makeQuery(id+"F0.imprint","IMPRINT",EDGE,{"derivedFrom":sQuery(id+"F0.wireOp",EDGE,"E0.rect.bottom")}),1.0]])]});
            var Q1;
            Q1=makeQuery(id+"F1.opExtrude","CAP_FACE",FACE,{"disambiguationData":[OSD([sQuery(id+"F0.wireOp",EDGE,"E0.rect.bottom"),sQuery(id+"F0.wireOp",EDGE,"E0.rect.top"),sQuery(id+"F0.wireOp",EDGE,"E0.rect.left"),sQuery(id+"F0.wireOp",EDGE,"E0.rect.right"),sQuery(id+"F0.wireOp",EDGE,"E10.0"),sQuery(id+"F0.wireOp",EDGE,"E10.1"),sQuery(id+"F0.wireOp",EDGE,"E10.2"),sQuery(id+"F0.wireOp",EDGE,"E10.3")])],"isStart":false});
            var Q2;
            Q2=makeQuery(id+"F0.imprint","IMPRINT",FACE,{"disambiguationData":[TD([[makeQuery(id+"F0.imprint","IMPRINT",EDGE,{"derivedFrom":sQuery(id+"F0.wireOp",EDGE,"E2.bottom")}),-1.0]])]});
            extrude(context, id + "F2", {"entities" : qUnion([Q0, Q1, Q2]), "operationType" : NewBodyOperationType.ADD, "depth" : 1 * mm});
        }
        {
            var Q0;
            Q0=makeQuery(id+"F2.opExtrude","CAP_FACE",FACE,{"disambiguationData":[OSD([sQuery(id+"F0.wireOp",EDGE,"E0.rect.bottom"),sQuery(id+"F0.wireOp",EDGE,"E0.rect.top"),sQuery(id+"F0.wireOp",EDGE,"E0.rect.left"),sQuery(id+"F0.wireOp",EDGE,"E0.rect.right")])],"isStart":false});
            var sketch = newSketch(context, id + "F3", { "sketchPlane" : qUnion([Q0])});
            skLineSegment(sketch, "E59.0", {"start": v(-10, -20) * mm, "end": v(-10, -30) * mm});
            skLineSegment(sketch, "E60.0", {"start": v(-10, -30) * mm, "end": v(-5, -30) * mm});
            skLineSegment(sketch, "E61.0", {"start": v(-5, -20) * mm, "end": v(-5, -30) * mm});
            skLineSegment(sketch, "E62.0", {"start": v(-10, -20) * mm, "end": v(-6, -20) * mm});
            skPoint(sketch, "E63.0", {"position": v(-6, -18.5) * mm});
            skLineSegment(sketch, "E64.0", {"start": v(-6, -20) * mm, "end": v(-6, -18.5) * mm});
            skLineSegment(sketch, "E65.0", {"start": v(-5, -20) * mm, "end": v(-5, -17.5) * mm});
            skArc(sketch, "E66.0", {"start": v(-5, -17.5) * mm, "mid": v(-5.15, -17.15) * mm, "end": v(-5.5, -17) * mm});
            skArc(sketch, "E67.0", {"start": v(-6, -18.5) * mm, "mid": v(-6.15, -18.15) * mm, "end": v(-6.5, -18) * mm});
            skLineSegment(sketch, "E68.0", {"start": v(-6.5, -18) * mm, "end": v(-9.5, -18) * mm});
            skLineSegment(sketch, "E69.0", {"start": v(-5.5, -17) * mm, "end": v(-8.5, -17) * mm});
            skArc(sketch, "E70.0", {"start": v(-9, -16.5) * mm, "mid": v(-8.85, -16.85) * mm, "end": v(-8.5, -17) * mm});
            skArc(sketch, "E71.0", {"start": v(-10, -17.5) * mm, "mid": v(-9.85, -17.85) * mm, "end": v(-9.5, -18) * mm});
            skLineSegment(sketch, "E72.0", {"start": v(-10, -17.5) * mm, "end": v(-10, -14.5) * mm});
            skLineSegment(sketch, "E73.0.2", {"start": v(-15, 37.5) * mm, "end": v(-15, -37.5) * mm});
            skLineSegment(sketch, "E74.0", {"start": v(-9, -16.5) * mm, "end": v(-9, -15) * mm});
            skLineSegment(sketch, "E75.0", {"start": v(-9, -15) * mm, "end": v(-1.5, -15) * mm});
            skArc(sketch, "E76.0", {"start": v(-9.5, -14) * mm, "mid": v(-9.85, -14.15) * mm, "end": v(-10, -14.5) * mm});
            skLineSegment(sketch, "E77.0", {"start": v(-9.5, -14) * mm, "end": v(-2.5, -14) * mm});
            skArc(sketch, "E78.0", {"start": v(-1.5, -15) * mm, "mid": v(-1.15, -14.85) * mm, "end": v(-1, -14.5) * mm});
            skArc(sketch, "E79.0", {"start": v(-2.5, -14) * mm, "mid": v(-2.15, -13.85) * mm, "end": v(-2, -13.5) * mm});
            skLineSegment(sketch, "E80.0.0", {"start": v(15, -37.5) * mm, "end": v(15, 37.5) * mm});
            skLineSegment(sketch, "E80.0.3", {"start": v(-15, -37.5) * mm, "end": v(15, -37.5) * mm});
            skLineSegment(sketch, "E81.0", {"start": v(-2, -13.5) * mm, "end": v(-2, -12.5) * mm});
            skLineSegment(sketch, "E82.0", {"start": v(-1, -14.5) * mm, "end": v(-1, -11.5) * mm});
            skArc(sketch, "E83.0", {"start": v(-1, -11.5) * mm, "mid": v(-1.15, -11.15) * mm, "end": v(-1.5, -11) * mm});
            skArc(sketch, "E84.0", {"start": v(-2, -12.5) * mm, "mid": v(-2.15, -12.15) * mm, "end": v(-2.5, -12) * mm});
            skLineSegment(sketch, "E85.0", {"start": v(-2.5, -12) * mm, "end": v(-9.5, -12) * mm});
            skLineSegment(sketch, "E86.0", {"start": v(-1.5, -11) * mm, "end": v(-9, -11) * mm});
            skArc(sketch, "E87.0", {"start": v(-10, -11.5) * mm, "mid": v(-9.85, -11.85) * mm, "end": v(-9.5, -12) * mm});
            skPoint(sketch, "E88.0", {"position": v(-10, -11) * mm});
            skLineSegment(sketch, "E89.0", {"start": v(-10, -11.5) * mm, "end": v(-10, -8.5) * mm});
            skLineSegment(sketch, "E90.0", {"start": v(-9, -9) * mm, "end": v(-9, -11) * mm});
            skLineSegment(sketch, "E91.0", {"start": v(-9, -9) * mm, "end": v(-1.5, -9) * mm});
            skArc(sketch, "E92.0", {"start": v(-9.5, -8) * mm, "mid": v(-9.85, -8.15) * mm, "end": v(-10, -8.5) * mm});
            skLineSegment(sketch, "E93.0.1", {"start": v(15, 37.5) * mm, "end": v(-15, 37.5) * mm});
            skLineSegment(sketch, "E94.0", {"start": v(-9.5, -8) * mm, "end": v(-2.5, -8) * mm});
            skArc(sketch, "E95.0", {"start": v(-2.5, -8) * mm, "mid": v(-2.15, -7.85) * mm, "end": v(-2, -7.5) * mm});
            skArc(sketch, "E96.0", {"start": v(-1.5, -9) * mm, "mid": v(-1.15, -8.85) * mm, "end": v(-1, -8.5) * mm});
            skLineSegment(sketch, "E97.0", {"start": v(-1, -8.5) * mm, "end": v(-1, -5.5) * mm});
            skLineSegment(sketch, "E98.0", {"start": v(-2, -7.5) * mm, "end": v(-2, -6.5) * mm});
            skArc(sketch, "E99.0", {"start": v(-2, -6.5) * mm, "mid": v(-2.15, -6.15) * mm, "end": v(-2.5, -6) * mm});
            skPoint(sketch, "E100.0", {"position": v(-1.5, -5) * mm});
            skArc(sketch, "E101.0", {"start": v(-1, -5.5) * mm, "mid": v(-1.15, -5.15) * mm, "end": v(-1.5, -5) * mm});
            skLineSegment(sketch, "E102.0", {"start": v(-1.5, -5) * mm, "end": v(-9, -5) * mm});
            skLineSegment(sketch, "E103.0", {"start": v(-2.5, -6) * mm, "end": v(-9.5, -6) * mm});
            skArc(sketch, "E104.0", {"start": v(-10, -5.5) * mm, "mid": v(-9.85, -5.85) * mm, "end": v(-9.5, -6) * mm});
            skLineSegment(sketch, "E105.0", {"start": v(-10, -5.5) * mm, "end": v(-10, -2.5) * mm});
            skLineSegment(sketch, "E106.0", {"start": v(-9, -3) * mm, "end": v(-9, -5) * mm});
            skArc(sketch, "E107.0", {"start": v(-9.5, -2) * mm, "mid": v(-9.85, -2.15) * mm, "end": v(-10, -2.5) * mm});
            skLineSegment(sketch, "E108.0", {"start": v(-9.5, -2) * mm, "end": v(-2.5, -2) * mm});
            skLineSegment(sketch, "E109.0", {"start": v(-9, -3) * mm, "end": v(-1.5, -3) * mm});
            skArc(sketch, "E110.0", {"start": v(-2.5, -2) * mm, "mid": v(-2.15, -1.85) * mm, "end": v(-2, -1.5) * mm});
            skArc(sketch, "E111.0", {"start": v(-1.5, -3) * mm, "mid": v(-1.15, -2.85) * mm, "end": v(-1, -2.5) * mm});
            skLineSegment(sketch, "E112.0", {"start": v(-1, -2.5) * mm, "end": v(-1, 0.5) * mm});
            skLineSegment(sketch, "E113.0", {"start": v(-2, -1.5) * mm, "end": v(-2, -0.5) * mm});
            skArc(sketch, "E114.0", {"start": v(-2, -0.5) * mm, "mid": v(-2.15, -0.15) * mm, "end": v(-2.5, 0) * mm});
            skArc(sketch, "E115.0", {"start": v(-1, 0.5) * mm, "mid": v(-1.15, 0.85) * mm, "end": v(-1.5, 1) * mm});
            skLineSegment(sketch, "E116.0", {"start": v(-1.5, 1) * mm, "end": v(-9, 1) * mm});
            skLineSegment(sketch, "E117.0", {"start": v(-2.5, 0) * mm, "end": v(-9.5, 0) * mm});
            skArc(sketch, "E118.0", {"start": v(-10, 0.5) * mm, "mid": v(-9.85, 0.15) * mm, "end": v(-9.5, 0) * mm});
            skLineSegment(sketch, "E119.0", {"start": v(-10, 0.5) * mm, "end": v(-10, 3.5) * mm});
            skLineSegment(sketch, "E120.0", {"start": v(-9, 3) * mm, "end": v(-9, 1) * mm});
            skArc(sketch, "E121.0", {"start": v(-9.5, 4) * mm, "mid": v(-9.85, 3.85) * mm, "end": v(-10, 3.5) * mm});
            skLineSegment(sketch, "E122.0", {"start": v(-9.5, 4) * mm, "end": v(-2.5, 4) * mm});
            skLineSegment(sketch, "E123.0", {"start": v(-9, 3) * mm, "end": v(-1.5, 3) * mm});
            skArc(sketch, "E124.0", {"start": v(-1.5, 3) * mm, "mid": v(-1.15, 3.15) * mm, "end": v(-1, 3.5) * mm});
            skArc(sketch, "E125.0", {"start": v(-2.5, 4) * mm, "mid": v(-2.15, 4.15) * mm, "end": v(-2, 4.5) * mm});
            skLineSegment(sketch, "E126.0", {"start": v(-2, 4.5) * mm, "end": v(-2, 5.5) * mm});
            skLineSegment(sketch, "E127.0", {"start": v(-1, 3.5) * mm, "end": v(-1, 6.5) * mm});
            skArc(sketch, "E128.0", {"start": v(-1, 6.5) * mm, "mid": v(-1.15, 6.85) * mm, "end": v(-1.5, 7) * mm});
            skArc(sketch, "E129.0", {"start": v(-2, 5.5) * mm, "mid": v(-2.15, 5.85) * mm, "end": v(-2.5, 6) * mm});
            skLineSegment(sketch, "E130.0", {"start": v(-2.5, 6) * mm, "end": v(-9.5, 6) * mm});
            skLineSegment(sketch, "E131.0", {"start": v(-1.5, 7) * mm, "end": v(-9, 7) * mm});
            skArc(sketch, "E132.0", {"start": v(-10, 6.5) * mm, "mid": v(-9.85, 6.15) * mm, "end": v(-9.5, 6) * mm});
            skPoint(sketch, "E133.0", {"position": v(-10, 7) * mm});
            skLineSegment(sketch, "E134.0", {"start": v(-9, 9) * mm, "end": v(-9, 7) * mm});
            skLineSegment(sketch, "E135.0", {"start": v(-10, 6.5) * mm, "end": v(-10, 9.5) * mm});
            skArc(sketch, "E136.0", {"start": v(-9.5, 10) * mm, "mid": v(-9.85, 9.85) * mm, "end": v(-10, 9.5) * mm});
            skLineSegment(sketch, "E137.0", {"start": v(-9.5, 10) * mm, "end": v(-2.5, 10) * mm});
            skLineSegment(sketch, "E138.0", {"start": v(-9, 9) * mm, "end": v(-1.5, 9) * mm});
            skArc(sketch, "E139.0", {"start": v(-2.5, 10) * mm, "mid": v(-2.15, 10.15) * mm, "end": v(-2, 10.5) * mm});
            skArc(sketch, "E140.0", {"start": v(-1.5, 9) * mm, "mid": v(-1.15, 9.15) * mm, "end": v(-1, 9.5) * mm});
            skLineSegment(sketch, "E141.0", {"start": v(-1, 9.5) * mm, "end": v(-1, 12.5) * mm});
            skLineSegment(sketch, "E142.0", {"start": v(-2, 10.5) * mm, "end": v(-2, 11.5) * mm});
            skArc(sketch, "E143.0", {"start": v(-2, 11.5) * mm, "mid": v(-2.15, 11.85) * mm, "end": v(-2.5, 12) * mm});
            skArc(sketch, "E144.0", {"start": v(-1, 12.5) * mm, "mid": v(-1.15, 12.85) * mm, "end": v(-1.5, 13) * mm});
            skLineSegment(sketch, "E145.0", {"start": v(-1.5, 13) * mm, "end": v(-9, 13) * mm});
            skLineSegment(sketch, "E146.0", {"start": v(-2.5, 12) * mm, "end": v(-9.5, 12) * mm});
            skArc(sketch, "E147.0", {"start": v(-10, 12.5) * mm, "mid": v(-9.85, 12.15) * mm, "end": v(-9.5, 12) * mm});
            skLineSegment(sketch, "E148.0", {"start": v(-10, 12.5) * mm, "end": v(-10, 15.5) * mm});
            skLineSegment(sketch, "E149.0", {"start": v(-9, 15) * mm, "end": v(-9, 13) * mm});
            skArc(sketch, "E150.0", {"start": v(-9.5, 16) * mm, "mid": v(-9.85, 15.85) * mm, "end": v(-10, 15.5) * mm});
            skLineSegment(sketch, "E151.0", {"start": v(-9.5, 16) * mm, "end": v(-2.5, 16) * mm});
            skLineSegment(sketch, "E152.0", {"start": v(-9, 15) * mm, "end": v(-1.5, 15) * mm});
            skArc(sketch, "E153.0", {"start": v(-2.5, 16) * mm, "mid": v(-2.15, 16.15) * mm, "end": v(-2, 16.5) * mm});
            skArc(sketch, "E154.0", {"start": v(-1.5, 15) * mm, "mid": v(-1.15, 15.15) * mm, "end": v(-1, 15.5) * mm});
            skLineSegment(sketch, "E155.0", {"start": v(-1, 15.5) * mm, "end": v(-1, 18.5) * mm});
            skPoint(sketch, "E156.0", {"position": v(-2, 17.5) * mm});
            skLineSegment(sketch, "E157.0", {"start": v(-2, 16.5) * mm, "end": v(-2, 17.5) * mm});
            skArc(sketch, "E158.0", {"start": v(-2, 17.5) * mm, "mid": v(-2.15, 17.85) * mm, "end": v(-2.5, 18) * mm});
            skArc(sketch, "E159.0", {"start": v(-1, 18.5) * mm, "mid": v(-1.15, 18.85) * mm, "end": v(-1.5, 19) * mm});
            skLineSegment(sketch, "E160.0", {"start": v(-1.5, 19) * mm, "end": v(-9, 19) * mm});
            skLineSegment(sketch, "E161.0", {"start": v(-2.5, 18) * mm, "end": v(-9.5, 18) * mm});
            skArc(sketch, "E162.0", {"start": v(-10, 18.5) * mm, "mid": v(-9.85, 18.15) * mm, "end": v(-9.5, 18) * mm});
            skLineSegment(sketch, "E163.0", {"start": v(-10, 18.5) * mm, "end": v(-10, 21.5) * mm});
            skLineSegment(sketch, "E164.0", {"start": v(-9, 21) * mm, "end": v(-9, 19) * mm});
            skArc(sketch, "E165.0", {"start": v(-9.5, 22) * mm, "mid": v(-9.85, 21.85) * mm, "end": v(-10, 21.5) * mm});
            skLineSegment(sketch, "E166.0", {"start": v(-9.5, 22) * mm, "end": v(-2.5, 22) * mm});
            skLineSegment(sketch, "E167.0", {"start": v(-9, 21) * mm, "end": v(-1.5, 21) * mm});
            skArc(sketch, "E168.0", {"start": v(-1.5, 21) * mm, "mid": v(-1.15, 21.15) * mm, "end": v(-1, 21.5) * mm});
            skArc(sketch, "E169.0", {"start": v(-2.5, 22) * mm, "mid": v(-2.15, 22.15) * mm, "end": v(-2, 22.5) * mm});
            skLineSegment(sketch, "E170.0", {"start": v(-2, 22.5) * mm, "end": v(-2, 23.5) * mm});
            skLineSegment(sketch, "E171.0", {"start": v(-1, 21.5) * mm, "end": v(-1, 24.5) * mm});
            skArc(sketch, "E172.0", {"start": v(-1, 24.5) * mm, "mid": v(-1.15, 24.85) * mm, "end": v(-1.5, 25) * mm});
            skArc(sketch, "E173.0", {"start": v(-2, 23.5) * mm, "mid": v(-2.15, 23.85) * mm, "end": v(-2.5, 24) * mm});
            skLineSegment(sketch, "E174.0", {"start": v(-1.5, 25) * mm, "end": v(-9, 25) * mm});
            skLineSegment(sketch, "E175.0", {"start": v(-2.5, 24) * mm, "end": v(-9.5, 24) * mm});
            skArc(sketch, "E176.0", {"start": v(-10, 24.5) * mm, "mid": v(-9.85, 24.15) * mm, "end": v(-9.5, 24) * mm});
            skLineSegment(sketch, "E177.0", {"start": v(-10, 24.5) * mm, "end": v(-10, 27.5) * mm});
            skLineSegment(sketch, "E178.0", {"start": v(-9, 32.11) * mm, "end": v(9.03, 32.26) * mm});
            skLineSegment(sketch, "E179.0", {"start": v(-9, 27) * mm, "end": v(-1.5, 27) * mm});
            skLineSegment(sketch, "E180.0", {"start": v(-9, 27) * mm, "end": v(-9, 25) * mm});
            skArc(sketch, "E181.0", {"start": v(-9.5, 28) * mm, "mid": v(-9.85, 27.85) * mm, "end": v(-10, 27.5) * mm});
            skLineSegment(sketch, "E182.0", {"start": v(-9.5, 28) * mm, "end": v(-2.5, 28) * mm});
            skArc(sketch, "E183.0", {"start": v(-1.5, 27) * mm, "mid": v(-1.15, 27.15) * mm, "end": v(-1, 27.5) * mm});
            skArc(sketch, "E184.0", {"start": v(-2.5, 28) * mm, "mid": v(-2.15, 28.15) * mm, "end": v(-2, 28.5) * mm});
            skLineSegment(sketch, "E185.0", {"start": v(-2, 28.5) * mm, "end": v(-2, 29.5) * mm});
            skLineSegment(sketch, "E186.0", {"start": v(-1, 27.5) * mm, "end": v(-1, 30.5) * mm});
            skArc(sketch, "E187.0", {"start": v(-1, 30.5) * mm, "mid": v(-1.15, 30.85) * mm, "end": v(-1.5, 31) * mm});
            skArc(sketch, "E188.0", {"start": v(-2, 29.5) * mm, "mid": v(-2.15, 29.85) * mm, "end": v(-2.5, 30) * mm});
            skLineSegment(sketch, "E189.0", {"start": v(-1.5, 31) * mm, "end": v(-9, 31) * mm});
            skLineSegment(sketch, "E190.0", {"start": v(-2.5, 30) * mm, "end": v(-9.5, 30) * mm});
            skArc(sketch, "E191.0", {"start": v(-10, 30.5) * mm, "mid": v(-9.85, 30.15) * mm, "end": v(-9.5, 30) * mm});
            skLineSegment(sketch, "E192.0", {"start": v(-10, 31) * mm, "end": v(-10, 33.22) * mm});
            skLineSegment(sketch, "E193.0", {"start": v(-10, 30.5) * mm, "end": v(-10, 31) * mm});
            skLineSegment(sketch, "E194.0", {"start": v(-9, 31) * mm, "end": v(-9, 32.11) * mm});
            skLineSegment(sketch, "E195.0", {"start": v(-10, 33.22) * mm, "end": v(7.5, 33.22) * mm});
            skLineSegment(sketch, "E196.0", {"start": v(0, 0) * mm, "end": v(0, 17.9) * mm, "construction": true});
            skArc(sketch, "E197.0.MirrorCS", {"start": v(2, -6.5) * mm, "mid": v(2.15, -6.15) * mm, "end": v(2.5, -6) * mm});
            skArc(sketch, "E197.1.MirrorCS", {"start": v(2.5, 28) * mm, "mid": v(2.15, 28.15) * mm, "end": v(2, 28.5) * mm});
            skArc(sketch, "E197.2.MirrorCS", {"start": v(1, 12.5) * mm, "mid": v(1.15, 12.85) * mm, "end": v(1.5, 13) * mm});
            skLineSegment(sketch, "E197.3.MirrorCS", {"start": v(1, 15.5) * mm, "end": v(1, 18.5) * mm});
            skLineSegment(sketch, "E197.4.MirrorCS", {"start": v(2, 4.5) * mm, "end": v(2, 5.5) * mm});
            skLineSegment(sketch, "E197.5.MirrorCS", {"start": v(2, 28.5) * mm, "end": v(2, 29.5) * mm});
            skArc(sketch, "E197.6.MirrorCS", {"start": v(2.5, 16) * mm, "mid": v(2.15, 16.15) * mm, "end": v(2, 16.5) * mm});
            skLineSegment(sketch, "E197.7.MirrorCS", {"start": v(1, -8.5) * mm, "end": v(1, -5.5) * mm});
            skArc(sketch, "E197.8.MirrorCS", {"start": v(2.5, -8) * mm, "mid": v(2.15, -7.85) * mm, "end": v(2, -7.5) * mm});
            skLineSegment(sketch, "E197.9.MirrorCS", {"start": v(2, 16.5) * mm, "end": v(2, 17.5) * mm});
            skArc(sketch, "E197.10.MirrorCS", {"start": v(2, 11.5) * mm, "mid": v(2.15, 11.85) * mm, "end": v(2.5, 12) * mm});
            skArc(sketch, "E197.11.MirrorCS", {"start": v(1.5, 9) * mm, "mid": v(1.15, 9.15) * mm, "end": v(1, 9.5) * mm});
            skArc(sketch, "E197.12.MirrorCS", {"start": v(1, -5.5) * mm, "mid": v(1.15, -5.15) * mm, "end": v(1.5, -5) * mm});
            skArc(sketch, "E197.13.MirrorCS", {"start": v(1.5, 27) * mm, "mid": v(1.15, 27.15) * mm, "end": v(1, 27.5) * mm});
            skArc(sketch, "E197.14.MirrorCS", {"start": v(1, 18.5) * mm, "mid": v(1.15, 18.85) * mm, "end": v(1.5, 19) * mm});
            skLineSegment(sketch, "E197.15.MirrorCS", {"start": v(2, 10.5) * mm, "end": v(2, 11.5) * mm});
            skArc(sketch, "E197.16.MirrorCS", {"start": v(2, 5.5) * mm, "mid": v(2.15, 5.85) * mm, "end": v(2.5, 6) * mm});
            skLineSegment(sketch, "E197.17.MirrorCS", {"start": v(2, -7.5) * mm, "end": v(2, -6.5) * mm});
            skArc(sketch, "E197.18.MirrorCS", {"start": v(2, 17.5) * mm, "mid": v(2.15, 17.85) * mm, "end": v(2.5, 18) * mm});
            skArc(sketch, "E197.19.MirrorCS", {"start": v(1.5, 15) * mm, "mid": v(1.15, 15.15) * mm, "end": v(1, 15.5) * mm});
            skLineSegment(sketch, "E197.20.MirrorCS", {"start": v(1, 9.5) * mm, "end": v(1, 12.5) * mm});
            skArc(sketch, "E197.21.MirrorCS", {"start": v(1.5, -9) * mm, "mid": v(1.15, -8.85) * mm, "end": v(1, -8.5) * mm});
            skArc(sketch, "E197.22.MirrorCS", {"start": v(2.5, 10) * mm, "mid": v(2.15, 10.15) * mm, "end": v(2, 10.5) * mm});
            skLineSegment(sketch, "E197.23.MirrorCS", {"start": v(10, 30.5) * mm, "end": v(10, 31) * mm});
            skArc(sketch, "E197.24.MirrorCS", {"start": v(2.5, 22) * mm, "mid": v(2.15, 22.15) * mm, "end": v(2, 22.5) * mm});
            skLineSegment(sketch, "E197.25.MirrorCS", {"start": v(5, -20) * mm, "end": v(5, -17.5) * mm});
            skLineSegment(sketch, "E197.26.MirrorCS", {"start": v(6, -20) * mm, "end": v(6, -18.5) * mm});
            skLineSegment(sketch, "E197.27.MirrorCS", {"start": v(9, 31) * mm, "end": v(9, 32.11) * mm});
            skArc(sketch, "E197.28.MirrorCS", {"start": v(2, 29.5) * mm, "mid": v(2.15, 29.85) * mm, "end": v(2.5, 30) * mm});
            skLineSegment(sketch, "E197.29.MirrorCS", {"start": v(2, 22.5) * mm, "end": v(2, 23.5) * mm});
            skLineSegment(sketch, "E197.30.MirrorCS", {"start": v(1, 27.5) * mm, "end": v(1, 30.5) * mm});
            skLineSegment(sketch, "E197.31.MirrorCS", {"start": v(6.5, -18) * mm, "end": v(9.5, -18) * mm});
            skLineSegment(sketch, "E197.32.MirrorCS", {"start": v(2, -13.5) * mm, "end": v(2, -12.5) * mm});
            skArc(sketch, "E197.33.MirrorCS", {"start": v(6, -18.5) * mm, "mid": v(6.15, -18.15) * mm, "end": v(6.5, -18) * mm});
            skArc(sketch, "E197.34.MirrorCS", {"start": v(9, -16.5) * mm, "mid": v(8.85, -16.85) * mm, "end": v(8.5, -17) * mm});
            skArc(sketch, "E197.35.MirrorCS", {"start": v(2, 23.5) * mm, "mid": v(2.15, 23.85) * mm, "end": v(2.5, 24) * mm});
            skArc(sketch, "E197.36.MirrorCS", {"start": v(9.5, -14) * mm, "mid": v(9.85, -14.15) * mm, "end": v(10, -14.5) * mm});
            skArc(sketch, "E197.37.MirrorCS", {"start": v(1.5, -3) * mm, "mid": v(1.15, -2.85) * mm, "end": v(1, -2.5) * mm});
            skLineSegment(sketch, "E197.38.MirrorCS", {"start": v(1, 3.5) * mm, "end": v(1, 6.5) * mm});
            skArc(sketch, "E197.39.MirrorCS", {"start": v(9.5, 4) * mm, "mid": v(9.85, 3.85) * mm, "end": v(10, 3.5) * mm});
            skLineSegment(sketch, "E197.40.MirrorCS", {"start": v(5.5, -17) * mm, "end": v(8.5, -17) * mm});
            skLineSegment(sketch, "E197.41.MirrorCS", {"start": v(10, -17.5) * mm, "end": v(10, -14.5) * mm});
            skArc(sketch, "E197.42.MirrorCS", {"start": v(10, -17.5) * mm, "mid": v(9.85, -17.85) * mm, "end": v(9.5, -18) * mm});
            skLineSegment(sketch, "E197.43.MirrorCS", {"start": v(9, 3) * mm, "end": v(9, 1) * mm});
            skLineSegment(sketch, "E197.44.MirrorCS", {"start": v(9, 15) * mm, "end": v(9, 13) * mm});
            skLineSegment(sketch, "E197.45.MirrorCS", {"start": v(2, -1.5) * mm, "end": v(2, -0.5) * mm});
            skArc(sketch, "E197.46.MirrorCS", {"start": v(10, 30.5) * mm, "mid": v(9.85, 30.15) * mm, "end": v(9.5, 30) * mm});
            skLineSegment(sketch, "E197.47.MirrorCS", {"start": v(10, 0.5) * mm, "end": v(10, 3.5) * mm});
            skArc(sketch, "E197.48.MirrorCS", {"start": v(10, 12.5) * mm, "mid": v(9.85, 12.15) * mm, "end": v(9.5, 12) * mm});
            skArc(sketch, "E197.49.MirrorCS", {"start": v(10, 0.5) * mm, "mid": v(9.85, 0.15) * mm, "end": v(9.5, 0) * mm});
            skArc(sketch, "E197.50.MirrorCS", {"start": v(2, -12.5) * mm, "mid": v(2.15, -12.15) * mm, "end": v(2.5, -12) * mm});
            skArc(sketch, "E197.51.MirrorCS", {"start": v(1, 30.5) * mm, "mid": v(1.15, 30.85) * mm, "end": v(1.5, 31) * mm});
            skLineSegment(sketch, "E197.52.MirrorCS", {"start": v(1, -2.5) * mm, "end": v(1, 0.5) * mm});
            skArc(sketch, "E197.53.MirrorCS", {"start": v(2.5, 4) * mm, "mid": v(2.15, 4.15) * mm, "end": v(2, 4.5) * mm});
            skArc(sketch, "E197.54.MirrorCS", {"start": v(1.5, 21) * mm, "mid": v(1.15, 21.15) * mm, "end": v(1, 21.5) * mm});
            skArc(sketch, "E197.55.MirrorCS", {"start": v(1, 0.5) * mm, "mid": v(1.15, 0.85) * mm, "end": v(1.5, 1) * mm});
            skArc(sketch, "E197.56.MirrorCS", {"start": v(1.5, 3) * mm, "mid": v(1.15, 3.15) * mm, "end": v(1, 3.5) * mm});
            skLineSegment(sketch, "E197.57.MirrorCS", {"start": v(9, -16.5) * mm, "end": v(9, -15) * mm});
            skLineSegment(sketch, "E197.58.MirrorCS", {"start": v(1, -14.5) * mm, "end": v(1, -11.5) * mm});
            skArc(sketch, "E197.59.MirrorCS", {"start": v(2.5, -2) * mm, "mid": v(2.15, -1.85) * mm, "end": v(2, -1.5) * mm});
            skArc(sketch, "E197.60.MirrorCS", {"start": v(1.5, -15) * mm, "mid": v(1.15, -14.85) * mm, "end": v(1, -14.5) * mm});
            skArc(sketch, "E197.61.MirrorCS", {"start": v(9.5, 10) * mm, "mid": v(9.85, 9.85) * mm, "end": v(10, 9.5) * mm});
            skArc(sketch, "E197.62.MirrorCS", {"start": v(9.5, -8) * mm, "mid": v(9.85, -8.15) * mm, "end": v(10, -8.5) * mm});
            skLineSegment(sketch, "E197.63.MirrorCS", {"start": v(10, 6.5) * mm, "end": v(10, 9.5) * mm});
            skArc(sketch, "E197.64.MirrorCS", {"start": v(10, 24.5) * mm, "mid": v(9.85, 24.15) * mm, "end": v(9.5, 24) * mm});
            skLineSegment(sketch, "E197.65.MirrorCS", {"start": v(9, -9) * mm, "end": v(9, -11) * mm});
            skArc(sketch, "E197.66.MirrorCS", {"start": v(10, 6.5) * mm, "mid": v(9.85, 6.15) * mm, "end": v(9.5, 6) * mm});
            skLineSegment(sketch, "E197.67.MirrorCS", {"start": v(9, 21) * mm, "end": v(9, 19) * mm});
            skArc(sketch, "E197.68.MirrorCS", {"start": v(9.5, 22) * mm, "mid": v(9.85, 21.85) * mm, "end": v(10, 21.5) * mm});
            skArc(sketch, "E197.69.MirrorCS", {"start": v(9.5, 28) * mm, "mid": v(9.85, 27.85) * mm, "end": v(10, 27.5) * mm});
            skLineSegment(sketch, "E197.70.MirrorCS", {"start": v(10, 12.5) * mm, "end": v(10, 15.5) * mm});
            skLineSegment(sketch, "E197.71.MirrorCS", {"start": v(1, 21.5) * mm, "end": v(1, 24.5) * mm});
            skArc(sketch, "E197.72.MirrorCS", {"start": v(9.5, -2) * mm, "mid": v(9.85, -2.15) * mm, "end": v(10, -2.5) * mm});
            skLineSegment(sketch, "E197.73.MirrorCS", {"start": v(10, 18.5) * mm, "end": v(10, 21.5) * mm});
            skLineSegment(sketch, "E197.74.MirrorCS", {"start": v(10, 24.5) * mm, "end": v(10, 27.5) * mm});
            skPoint(sketch, "E197.75.MirrorP", {"position": v(6, -18.5) * mm});
            skPoint(sketch, "E197.76.MirrorP", {"position": v(2, 17.5) * mm});
            skLineSegment(sketch, "E197.77.MirrorCS", {"start": v(10, -20) * mm, "end": v(6, -20) * mm});
            skLineSegment(sketch, "E197.78.MirrorCS", {"start": v(9, -3) * mm, "end": v(9, -5) * mm});
            skLineSegment(sketch, "E197.79.MirrorCS", {"start": v(10, 31) * mm, "end": v(10, 33.22) * mm});
            skLineSegment(sketch, "E197.80.MirrorCS", {"start": v(10, -5.5) * mm, "end": v(10, -2.5) * mm});
            skArc(sketch, "E197.81.MirrorCS", {"start": v(10, -5.5) * mm, "mid": v(9.85, -5.85) * mm, "end": v(9.5, -6) * mm});
            skLineSegment(sketch, "E197.82.MirrorCS", {"start": v(10, -11.5) * mm, "end": v(10, -8.5) * mm});
            skArc(sketch, "E197.83.MirrorCS", {"start": v(10, -11.5) * mm, "mid": v(9.85, -11.85) * mm, "end": v(9.5, -12) * mm});
            skPoint(sketch, "E197.84.MirrorP", {"position": v(1.5, -5) * mm});
            skLineSegment(sketch, "E197.85.MirrorCS", {"start": v(9, 9) * mm, "end": v(9, 7) * mm});
            skLineSegment(sketch, "E197.86.MirrorCS", {"start": v(9.5, -2) * mm, "end": v(2.5, -2) * mm});
            skLineSegment(sketch, "E197.87.MirrorCS", {"start": v(9.5, -8) * mm, "end": v(2.5, -8) * mm});
            skLineSegment(sketch, "E197.88.MirrorCS", {"start": v(2.5, -12) * mm, "end": v(9.5, -12) * mm});
            skArc(sketch, "E197.89.MirrorCS", {"start": v(2.5, -14) * mm, "mid": v(2.15, -13.85) * mm, "end": v(2, -13.5) * mm});
            skPoint(sketch, "E197.90.MirrorP", {"position": v(10, 7) * mm});
            skLineSegment(sketch, "E197.91.MirrorCS", {"start": v(5, -20) * mm, "end": v(5, -30) * mm});
            skLineSegment(sketch, "E197.92.MirrorCS", {"start": v(9, 15) * mm, "end": v(1.5, 15) * mm});
            skLineSegment(sketch, "E197.93.MirrorCS", {"start": v(9, 3) * mm, "end": v(1.5, 3) * mm});
            skLineSegment(sketch, "E197.94.MirrorCS", {"start": v(10, -20) * mm, "end": v(10, -30) * mm});
            skArc(sketch, "E197.95.MirrorCS", {"start": v(5, -17.5) * mm, "mid": v(5.15, -17.15) * mm, "end": v(5.5, -17) * mm});
            skLineSegment(sketch, "E197.96.MirrorCS", {"start": v(10, -30) * mm, "end": v(5, -30) * mm});
            skLineSegment(sketch, "E197.97.MirrorCS", {"start": v(1.5, 1) * mm, "end": v(9, 1) * mm});
            skArc(sketch, "E197.98.MirrorCS", {"start": v(10, 18.5) * mm, "mid": v(9.85, 18.15) * mm, "end": v(9.5, 18) * mm});
            skLineSegment(sketch, "E197.99.MirrorCS", {"start": v(1.5, 13) * mm, "end": v(9, 13) * mm});
            skLineSegment(sketch, "E197.100.MirrorCS", {"start": v(9.5, 10) * mm, "end": v(2.5, 10) * mm});
            skLineSegment(sketch, "E197.101.MirrorCS", {"start": v(9.5, 4) * mm, "end": v(2.5, 4) * mm});
            skLineSegment(sketch, "E197.102.MirrorCS", {"start": v(9.5, 16) * mm, "end": v(2.5, 16) * mm});
            skLineSegment(sketch, "E197.103.MirrorCS", {"start": v(1.5, 19) * mm, "end": v(9, 19) * mm});
            skLineSegment(sketch, "E197.104.MirrorCS", {"start": v(1.5, 31) * mm, "end": v(9, 31) * mm});
            skArc(sketch, "E197.105.MirrorCS", {"start": v(2, -0.5) * mm, "mid": v(2.15, -0.15) * mm, "end": v(2.5, 0) * mm});
            skLineSegment(sketch, "E197.106.MirrorCS", {"start": v(1.5, -11) * mm, "end": v(9, -11) * mm});
            skArc(sketch, "E197.107.MirrorCS", {"start": v(9.5, 16) * mm, "mid": v(9.85, 15.85) * mm, "end": v(10, 15.5) * mm});
            skLineSegment(sketch, "E197.108.MirrorCS", {"start": v(9, 21) * mm, "end": v(1.5, 21) * mm});
            skLineSegment(sketch, "E197.109.MirrorCS", {"start": v(9.5, 28) * mm, "end": v(2.5, 28) * mm});
            skLineSegment(sketch, "E197.110.MirrorCS", {"start": v(9.5, 22) * mm, "end": v(2.5, 22) * mm});
            skLineSegment(sketch, "E197.111.MirrorCS", {"start": v(2.5, 24) * mm, "end": v(9.5, 24) * mm});
            skLineSegment(sketch, "E197.112.MirrorCS", {"start": v(2.5, -6) * mm, "end": v(9.5, -6) * mm});
            skLineSegment(sketch, "E197.113.MirrorCS", {"start": v(9, 27) * mm, "end": v(9, 25) * mm});
            skLineSegment(sketch, "E197.114.MirrorCS", {"start": v(2.5, 6) * mm, "end": v(9.5, 6) * mm});
            skLineSegment(sketch, "E197.115.MirrorCS", {"start": v(1.5, -5) * mm, "end": v(9, -5) * mm});
            skLineSegment(sketch, "E197.116.MirrorCS", {"start": v(1.5, 7) * mm, "end": v(9, 7) * mm});
            skLineSegment(sketch, "E197.117.MirrorCS", {"start": v(2.5, 30) * mm, "end": v(9.5, 30) * mm});
            skLineSegment(sketch, "E197.118.MirrorCS", {"start": v(9, -3) * mm, "end": v(1.5, -3) * mm});
            skLineSegment(sketch, "E197.119.MirrorCS", {"start": v(1.5, 25) * mm, "end": v(9, 25) * mm});
            skPoint(sketch, "E197.120.MirrorP", {"position": v(10, -11) * mm});
            skLineSegment(sketch, "E197.121.MirrorCS", {"start": v(9, 9) * mm, "end": v(1.5, 9) * mm});
            skLineSegment(sketch, "E197.122.MirrorCS", {"start": v(2.5, 0) * mm, "end": v(9.5, 0) * mm});
            skLineSegment(sketch, "E197.123.MirrorCS", {"start": v(9, -9) * mm, "end": v(1.5, -9) * mm});
            skLineSegment(sketch, "E197.124.MirrorCS", {"start": v(2.5, 12) * mm, "end": v(9.5, 12) * mm});
            skLineSegment(sketch, "E197.125.MirrorCS", {"start": v(9, -15) * mm, "end": v(1.5, -15) * mm});
            skLineSegment(sketch, "E197.126.MirrorCS", {"start": v(2.5, 18) * mm, "end": v(9.5, 18) * mm});
            skLineSegment(sketch, "E197.127.MirrorCS", {"start": v(9, 27) * mm, "end": v(1.5, 27) * mm});
            skLineSegment(sketch, "E197.128.MirrorCS", {"start": v(9.5, -14) * mm, "end": v(2.5, -14) * mm});
            skArc(sketch, "E198.30.MirrorCS", {"start": v(1, 6.5) * mm, "mid": v(1.15, 6.85) * mm, "end": v(1.5, 7) * mm});
            skArc(sketch, "E198.37.MirrorCS", {"start": v(1, -11.5) * mm, "mid": v(1.15, -11.15) * mm, "end": v(1.5, -11) * mm});
            skArc(sketch, "E198.38.MirrorCS", {"start": v(1, 24.5) * mm, "mid": v(1.15, 24.85) * mm, "end": v(1.5, 25) * mm});
            skLineSegment(sketch, "E199", {"start": v(7.5, 33.22) * mm, "end": v(10, 33.22) * mm});
            skLineSegment(sketch, "E200", {"start": v(9, 32.07) * mm, "end": v(8.93, 32.27) * mm});
            skSolve(sketch);
        }
        {
            var Q0;
            Q0=makeQuery(id+"F3.imprint","IMPRINT",FACE,{"disambiguationData":[TD([[makeQuery(id+"F3.imprint","IMPRINT",EDGE,{"derivedFrom":sQuery(id+"F3.wireOp",EDGE,"E59.0")}),1.0]])]});
            extrude(context, id + "F4", {"entities" : qUnion([Q0]), "operationType" : NewBodyOperationType.ADD, "depth" : 1 * mm});
        }
    });
